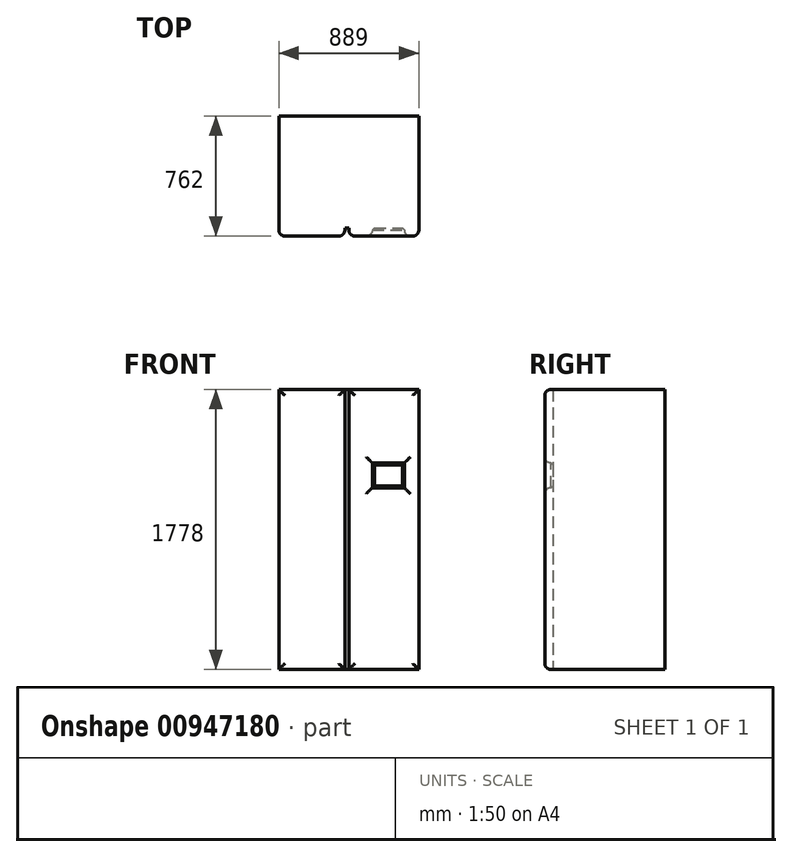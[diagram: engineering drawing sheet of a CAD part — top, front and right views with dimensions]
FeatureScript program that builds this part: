
annotation { "Feature Type Name" : "Feature", "Feature Type Description" : "" }
export const myFeature = defineFeature(function(context is Context, id is Id, definition is map)
    precondition{}
    {
        {
            var Q0;
            Q0=qCreatedBy(makeId("Top.planeOp"),FACE);
            var sketch = newSketch(context, id + "F0", { "sketchPlane" : qUnion([Q0])});
            skLineSegment(sketch, "E0.bottom", {"start": v(0, 0) * mm, "end": v(889, 0) * mm});
            skLineSegment(sketch, "E0.top", {"start": v(0, 762) * mm, "end": v(889, 762) * mm});
            skLineSegment(sketch, "E0.left", {"start": v(0, 0) * mm, "end": v(0, 762) * mm});
            skLineSegment(sketch, "E0.right", {"start": v(889, 0) * mm, "end": v(889, 762) * mm});
            skSolve(sketch);
        }
        {
            var Q0;
            Q0 = qSketchRegion(id + "F0", true);
            extrude(context, id + "F1", {"entities" : qUnion([Q0]), "depth" : 1778 * mm, "offsetDistance" : 25.4 * mm});
        }
        {
            var Q0;
            Q0=makeQuery(id+"F1.opExtrude","SWEPT_FACE",FACE,{"disambiguationData":[OSD([sQuery(id+"F0.wireOp",EDGE,"E0.bottom")])]});
            var sketch = newSketch(context, id + "F2", { "sketchPlane" : qUnion([Q0])});
            skLineSegment(sketch, "E1.bottom", {"start": v(419.1, 1778) * mm, "end": v(444.5, 1778) * mm});
            skLineSegment(sketch, "E1.top", {"start": v(419.1, 0) * mm, "end": v(444.5, 0) * mm});
            skLineSegment(sketch, "E1.left", {"start": v(419.1, 1778) * mm, "end": v(419.1, 0) * mm});
            skLineSegment(sketch, "E1.right", {"start": v(444.5, 1778) * mm, "end": v(444.5, 0) * mm});
            skSolve(sketch);
        }
        {
            var Q0;
            Q0 = qSketchRegion(id + "F2", true);
            extrude(context, id + "F3", {"entities" : qUnion([Q0]), "operationType" : NewBodyOperationType.REMOVE, "oppositeDirection" : true, "depth" : 50.8 * mm, "offsetDistance" : 25.4 * mm});
        }
        {
            var Q0;
            {var subQ0=sQuery(id+"F0.wireOp",EDGE,"E0.right");var subQ3=sQuery(id+"F0.wireOp",EDGE,"E0.bottom");Q0=makeQuery(id+"F3.boolean.opBoolean","SPLIT",FACE,{"disambiguationData":[TD([makeQuery(id+"F1.opExtrude","SWEPT_FACE",FACE,{"disambiguationData":[OSD([subQ0])]})])],"derivedFrom":makeQuery(id+"F1.opExtrude","SWEPT_FACE",FACE,{"disambiguationData":[OSD([subQ3])]})});}
            var sketch = newSketch(context, id + "F4", { "sketchPlane" : qUnion([Q0])});
            skLineSegment(sketch, "E2.bottom", {"start": v(593.74, 1311.37) * mm, "end": v(796.83, 1311.37) * mm});
            skLineSegment(sketch, "E2.top", {"start": v(593.74, 1153.8) * mm, "end": v(796.83, 1153.8) * mm});
            skLineSegment(sketch, "E2.left", {"start": v(593.74, 1311.37) * mm, "end": v(593.74, 1153.8) * mm});
            skLineSegment(sketch, "E2.right", {"start": v(796.83, 1311.37) * mm, "end": v(796.83, 1153.8) * mm});
            skSolve(sketch);
        }
        {
            var Q0;
            Q0=makeQuery(id+"F4.imprint","IMPRINT",FACE,{"disambiguationData":[TD([[makeQuery(id+"F4.imprint","IMPRINT",EDGE,{"derivedFrom":sQuery(id+"F4.wireOp",EDGE,"E2.bottom")}),-1.0]])]});
            extrude(context, id + "F5", {"entities" : qUnion([Q0]), "operationType" : NewBodyOperationType.REMOVE, "oppositeDirection" : true, "depth" : 50.8 * mm, "offsetDistance" : 25.4 * mm});
        }
        {
            var Q0;
            Q0=makeQuery(id+"F5.boolean.opBoolean","COPY",FACE,{"derivedFrom":makeQuery(id+"F5.opExtrude","CAP_FACE",FACE,{"disambiguationData":[OSD([sQuery(id+"F4.wireOp",EDGE,"E2.bottom"),sQuery(id+"F4.wireOp",EDGE,"E2.top"),sQuery(id+"F4.wireOp",EDGE,"E2.left"),sQuery(id+"F4.wireOp",EDGE,"E2.right")])],"isStart":false})});
            chamfer(context, id + "F6", {"entities" : qUnion([Q0]), "width" : 12.7 * mm, "tangentPropagation" : true});
        }
        {
            var Q0;
            {var subQ1=sQuery(id+"F0.wireOp",EDGE,"E0.left");var subQ3=sQuery(id+"F0.wireOp",EDGE,"E0.bottom");Q0=makeQuery(id+"F3.boolean.opBoolean","SPLIT",FACE,{"disambiguationData":[TD([makeQuery(id+"F1.opExtrude","SWEPT_FACE",FACE,{"disambiguationData":[OSD([subQ1])]})])],"derivedFrom":makeQuery(id+"F1.opExtrude","SWEPT_FACE",FACE,{"disambiguationData":[OSD([subQ3])]})});}
            var Q1;
            {var subQ0=sQuery(id+"F0.wireOp",EDGE,"E0.right");var subQ3=sQuery(id+"F0.wireOp",EDGE,"E0.bottom");Q1=makeQuery(id+"F3.boolean.opBoolean","SPLIT",FACE,{"disambiguationData":[TD([makeQuery(id+"F1.opExtrude","SWEPT_FACE",FACE,{"disambiguationData":[OSD([subQ0])]})])],"derivedFrom":makeQuery(id+"F1.opExtrude","SWEPT_FACE",FACE,{"disambiguationData":[OSD([subQ3])]})});}
            fillet(context, id + "F7", {"entities" : qUnion([Q0, Q1]), "radius" : 38.1 * mm, "tangentPropagation" : true, "allowEdgeOverflow" : false});
        }
    });
